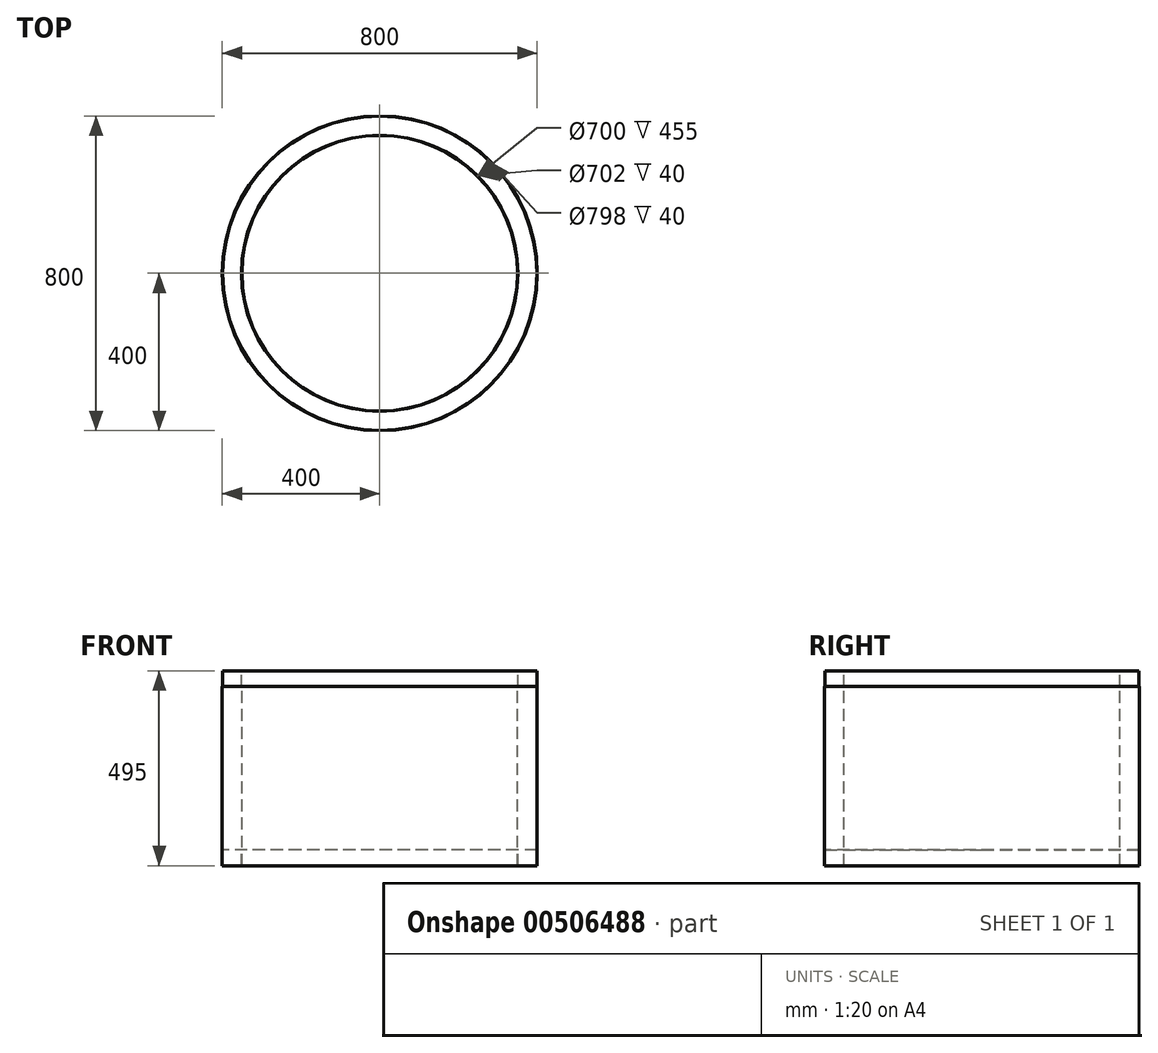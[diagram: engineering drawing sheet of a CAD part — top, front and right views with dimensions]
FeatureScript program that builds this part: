
annotation { "Feature Type Name" : "Feature", "Feature Type Description" : "" }
export const myFeature = defineFeature(function(context is Context, id is Id, definition is map)
    precondition{}
    {
        {
            var Q0;
            Q0=qCreatedBy(makeId("Front.planeOp"),FACE);
            var sketch = newSketch(context, id + "F0", { "sketchPlane" : qUnion([Q0])});
            skLineSegment(sketch, "E0", {"start": v(0, 74.87) * mm, "end": v(0, -73.71) * mm, "construction": true});
            skLineSegment(sketch, "E1", {"start": v(0, 374.84) * mm, "end": v(0, -528.94) * mm, "construction": true});
            skLineSegment(sketch, "E2", {"start": v(-350, -489.75) * mm, "end": v(-350, -34.75) * mm});
            skLineSegment(sketch, "E3", {"start": v(-350, -34.75) * mm, "end": v(-351, -34.75) * mm});
            skLineSegment(sketch, "E4", {"start": v(-351, -34.75) * mm, "end": v(-351, 5.25) * mm});
            skLineSegment(sketch, "E5", {"start": v(-351, 5.25) * mm, "end": v(-399, 5.25) * mm});
            skLineSegment(sketch, "E6", {"start": v(-399, 5.25) * mm, "end": v(-399, -34.75) * mm});
            skLineSegment(sketch, "E7", {"start": v(-399, -34.75) * mm, "end": v(-400, -34.75) * mm});
            skLineSegment(sketch, "E8", {"start": v(-400, -34.75) * mm, "end": v(-400, -489.75) * mm});
            skLineSegment(sketch, "E9", {"start": v(-400, -489.75) * mm, "end": v(-399, -489.75) * mm});
            skLineSegment(sketch, "E10", {"start": v(-399, -489.75) * mm, "end": v(-399, -449.75) * mm});
            skLineSegment(sketch, "E11", {"start": v(-399, -449.75) * mm, "end": v(-351, -449.75) * mm});
            skLineSegment(sketch, "E12", {"start": v(-351, -449.75) * mm, "end": v(-351, -489.75) * mm});
            skLineSegment(sketch, "E13", {"start": v(-351, -489.75) * mm, "end": v(-350, -489.75) * mm});
            skSolve(sketch);
        }
        {
            var Q0;
            Q0=qSketchRegion(id+"F0",true);
            var Q1;
            Q1=sQuery(id+"F0.wireOp",EDGE,"E1");
            revolve(context, id + "F1", {"entities" : qUnion([Q0]), "axis" : qUnion([Q1]), "revolveType" : RevolveType.FULL});
        }
    });
